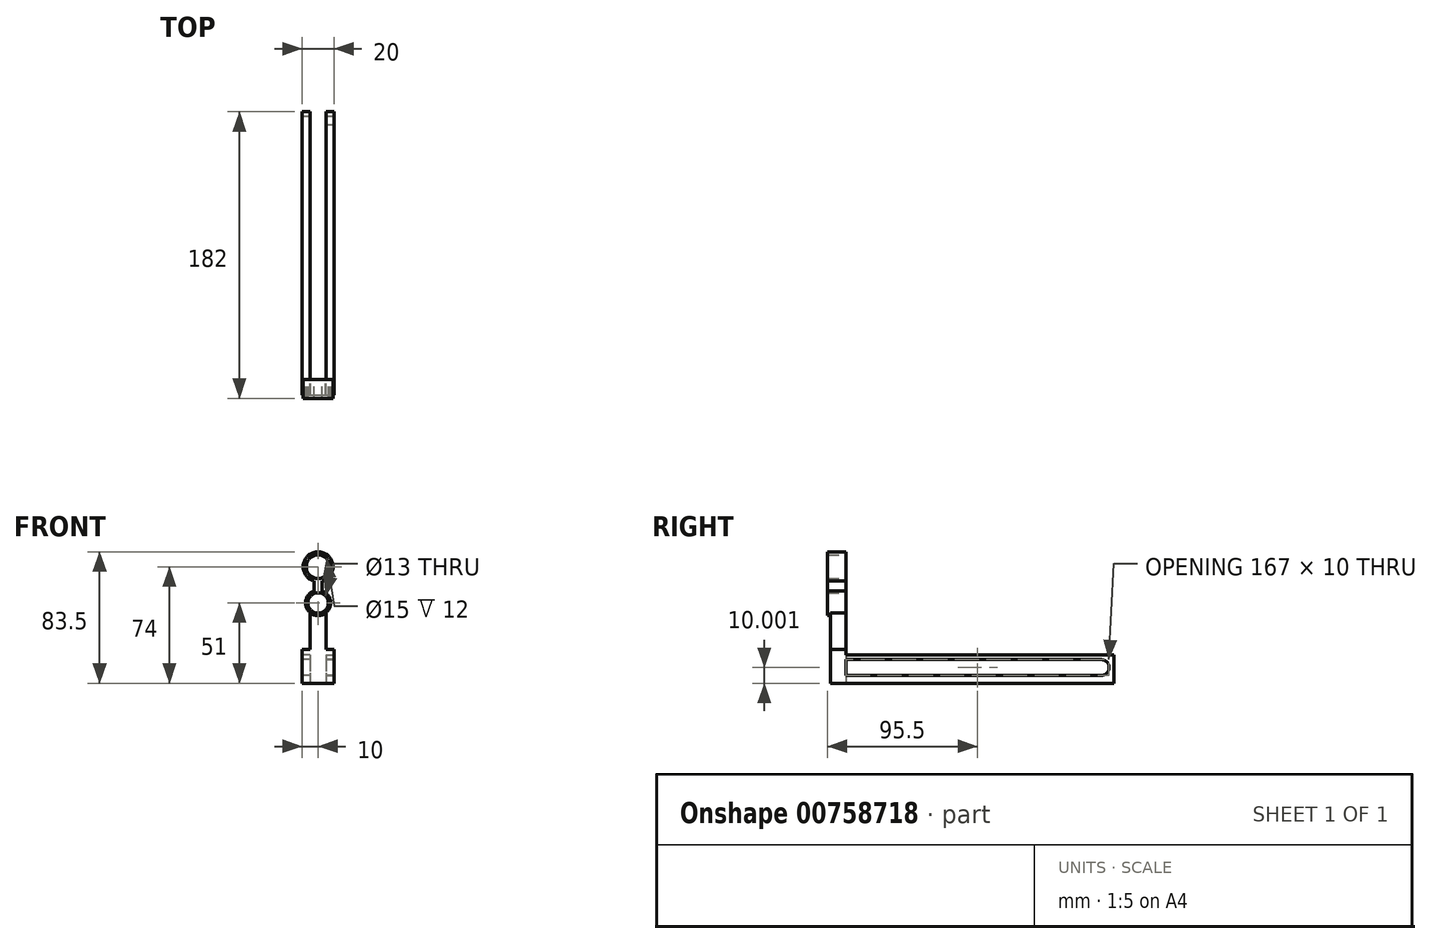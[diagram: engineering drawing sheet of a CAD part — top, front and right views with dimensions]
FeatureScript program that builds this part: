
annotation { "Feature Type Name" : "Feature", "Feature Type Description" : "" }
export const myFeature = defineFeature(function(context is Context, id is Id, definition is map)
    precondition{}
    {
        {
            var Q0;
            Q0=qCreatedBy(makeId("Front.planeOp"),FACE);
            var sketch = newSketch(context, id + "F0", { "sketchPlane" : qUnion([Q0])});
            skLineSegment(sketch, "E0", {"start": v(0, 0) * mm, "end": v(0, 23) * mm});
            skCircle(sketch, "E1", {"center": v(0, 23) * mm, "radius": 7.5 * mm});
            skCircle(sketch, "E2", {"center": v(0, 0) * mm, "radius": 6.5 * mm});
            skCircle(sketch, "E3", {"center": v(0, 23) * mm, "radius": 9.5 * mm});
            skCircle(sketch, "E4", {"center": v(0, 0) * mm, "radius": 8 * mm});
            skLineSegment(sketch, "E5", {"start": v(0, 0) * mm, "end": v(2.5, 0) * mm});
            skLineSegment(sketch, "E6", {"start": v(0, 0) * mm, "end": v(-2.5, 0) * mm});
            skLineSegment(sketch, "E7", {"start": v(-2.5, 0) * mm, "end": v(-2.5, 14.83) * mm});
            skLineSegment(sketch, "E8", {"start": v(-2.5, 14.83) * mm, "end": v(2.5, 14.83) * mm});
            skLineSegment(sketch, "E9", {"start": v(2.5, 14.83) * mm, "end": v(2.5, 0) * mm});
            skSolve(sketch);
        }
        {
            var Q0;
            Q0=makeQuery(id+"F0.imprint","IMPRINT",FACE,{"disambiguationData":[TD([[makeQuery(id+"F0.imprint","IMPRINT",EDGE,{"derivedFrom":sQuery(id+"F0.wireOp",EDGE,"E2")}),-1.0]])]});
            var Q1;
            {var subQ0=sQuery(id+"F0.wireOp",EDGE,"E3");var subQ1=sQuery(id+"F0.wireOp",EDGE,"E0");var subQ2=makeQuery(id+"F0.imprint","INTERSECT",VERTEX,{"derivedFrom":[subQ1,subQ0]});Q1=makeQuery(id+"F0.imprint","IMPRINT",FACE,{"disambiguationData":[TD([[makeQuery(id+"F0.imprint","IMPRINT",EDGE,{"disambiguationData":[TD([[subQ2,-1.0]])],"derivedFrom":subQ1}),1.0]])]});}
            var Q2;
            {var subQ0=sQuery(id+"F0.wireOp",EDGE,"E3");var subQ1=sQuery(id+"F0.wireOp",EDGE,"E0");var subQ2=makeQuery(id+"F0.imprint","INTERSECT",VERTEX,{"derivedFrom":[subQ1,subQ0]});Q2=makeQuery(id+"F0.imprint","IMPRINT",FACE,{"disambiguationData":[TD([[makeQuery(id+"F0.imprint","IMPRINT",EDGE,{"disambiguationData":[TD([[subQ2,-1.0]])],"derivedFrom":subQ1}),-1.0]])]});}
            var Q3;
            Q3=makeQuery(id+"F0.imprint","IMPRINT",FACE,{"disambiguationData":[TD([[makeQuery(id+"F0.imprint","IMPRINT",EDGE,{"derivedFrom":sQuery(id+"F0.wireOp",EDGE,"E1")}),-1.0]])]});
            var Q4;
            {var subQ0=sQuery(id+"F0.wireOp",EDGE,"E4");var subQ1=sQuery(id+"F0.wireOp",EDGE,"E0");var subQ2=makeQuery(id+"F0.imprint","INTERSECT",VERTEX,{"derivedFrom":[subQ1,subQ0]});Q4=makeQuery(id+"F0.imprint","IMPRINT",FACE,{"disambiguationData":[TD([[makeQuery(id+"F0.imprint","IMPRINT",EDGE,{"disambiguationData":[TD([[subQ2,-1.0]])],"derivedFrom":subQ1}),-1.0]])]});}
            var Q5;
            {var subQ0=sQuery(id+"F0.wireOp",EDGE,"E4");var subQ1=sQuery(id+"F0.wireOp",EDGE,"E0");var subQ2=makeQuery(id+"F0.imprint","INTERSECT",VERTEX,{"derivedFrom":[subQ1,subQ0]});Q5=makeQuery(id+"F0.imprint","IMPRINT",FACE,{"disambiguationData":[TD([[makeQuery(id+"F0.imprint","IMPRINT",EDGE,{"disambiguationData":[TD([[subQ2,-1.0]])],"derivedFrom":subQ1}),1.0]])]});}
            extrude(context, id + "F1", {"entities" : qUnion([Q0, Q1, Q2, Q3, Q4, Q5]), "depth" : 12 * mm, "offsetDistance" : 25 * mm});
        }
        {
            var Q0;
            Q0=qCreatedBy(makeId("Front.planeOp"),FACE);
            var sketch = newSketch(context, id + "F2", { "sketchPlane" : qUnion([Q0])});
            skLineSegment(sketch, "E10", {"start": v(0, 0) * mm, "end": v(0, -6.5) * mm});
            skLineSegment(sketch, "E11", {"start": v(0, -6.5) * mm, "end": v(10, -6.5) * mm});
            skLineSegment(sketch, "E12", {"start": v(0, -6.5) * mm, "end": v(-10, -6.5) * mm});
            skLineSegment(sketch, "E13", {"start": v(-10, -6.5) * mm, "end": v(-10, -51) * mm});
            skLineSegment(sketch, "E14", {"start": v(-10, -51) * mm, "end": v(10, -51) * mm});
            skLineSegment(sketch, "E15", {"start": v(10, -51) * mm, "end": v(10, -6.5) * mm});
            skLineSegment(sketch, "E16", {"start": v(-17.83, 0) * mm, "end": v(-17.83, -51) * mm});
            skLineSegment(sketch, "E17", {"start": v(-10, -51) * mm, "end": v(-17.83, -51) * mm});
            skLineSegment(sketch, "E18", {"start": v(0, -6.5) * mm, "end": v(5, -6.5) * mm});
            skLineSegment(sketch, "E19", {"start": v(5, -6.5) * mm, "end": v(5, -29.5) * mm});
            skLineSegment(sketch, "E20", {"start": v(5, -29.5) * mm, "end": v(10, -29.5) * mm});
            skLineSegment(sketch, "E21", {"start": v(-5, -6.5) * mm, "end": v(-5, -29.5) * mm});
            skLineSegment(sketch, "E22", {"start": v(-5, -29.5) * mm, "end": v(-10, -29.5) * mm});
            skSolve(sketch);
        }
        {
            var Q0;
            {var subQ0=sQuery(id+"F2.wireOp",EDGE,"E14");Q0=makeQuery(id+"F2.imprint","IMPRINT",FACE,{"disambiguationData":[TD([[makeQuery(id+"F2.imprint","IMPRINT",EDGE,{"derivedFrom":subQ0}),1.0]])]});}
            extrude(context, id + "F3", {"entities" : qUnion([Q0]), "operationType" : NewBodyOperationType.ADD, "depth" : 10 * mm, "offsetDistance" : 25 * mm});
        }
        {
            var Q0;
            Q0=qCreatedBy(makeId("Front.planeOp"),FACE);
            var sketch = newSketch(context, id + "F4", { "sketchPlane" : qUnion([Q0])});
            skLineSegment(sketch, "E23", {"start": v(0, 0) * mm, "end": v(5, 0) * mm});
            skLineSegment(sketch, "E24", {"start": v(0, 0) * mm, "end": v(-5, 0) * mm});
            skLineSegment(sketch, "E25", {"start": v(-5, 0) * mm, "end": v(-5, -46) * mm});
            skLineSegment(sketch, "E26", {"start": v(5, 0) * mm, "end": v(5, -46) * mm});
            skLineSegment(sketch, "E27", {"start": v(5, -46) * mm, "end": v(-5, -46) * mm});
            skLineSegment(sketch, "E28", {"start": v(5, -36) * mm, "end": v(-5, -36) * mm});
            skLineSegment(sketch, "E29", {"start": v(0, -36) * mm, "end": v(0, -46) * mm});
            skLineSegment(sketch, "E30", {"start": v(5, -46) * mm, "end": v(10, -46) * mm});
            skLineSegment(sketch, "E31", {"start": v(5, -36) * mm, "end": v(10, -36) * mm});
            skLineSegment(sketch, "E32", {"start": v(10, -36) * mm, "end": v(10, -46) * mm});
            skLineSegment(sketch, "E33", {"start": v(-5, -36) * mm, "end": v(-10, -36) * mm});
            skLineSegment(sketch, "E34", {"start": v(-5, -46) * mm, "end": v(-10, -46) * mm});
            skLineSegment(sketch, "E35", {"start": v(0, -36) * mm, "end": v(0, -33) * mm});
            skLineSegment(sketch, "E36", {"start": v(0, -33) * mm, "end": v(-10, -33) * mm});
            skLineSegment(sketch, "E37", {"start": v(0, -33) * mm, "end": v(10, -33) * mm});
            skLineSegment(sketch, "E38", {"start": v(10, -36) * mm, "end": v(10, -33) * mm});
            skLineSegment(sketch, "E39", {"start": v(-10, -36) * mm, "end": v(-10, -33) * mm});
            skLineSegment(sketch, "E40", {"start": v(5, -46) * mm, "end": v(5, -51) * mm});
            skLineSegment(sketch, "E41", {"start": v(5, -51) * mm, "end": v(10, -51) * mm});
            skLineSegment(sketch, "E42", {"start": v(10, -51) * mm, "end": v(10, -46) * mm});
            skLineSegment(sketch, "E43", {"start": v(-5, -46) * mm, "end": v(-5, -51) * mm});
            skLineSegment(sketch, "E44", {"start": v(-5, -51) * mm, "end": v(-10, -51) * mm});
            skLineSegment(sketch, "E45", {"start": v(-10, -51) * mm, "end": v(-10, -46) * mm});
            skSolve(sketch);
        }
        {
            var Q0;
            Q0=makeQuery(id+"F4.imprint","IMPRINT",FACE,{"disambiguationData":[TD([[makeQuery(id+"F4.imprint","IMPRINT",EDGE,{"derivedFrom":sQuery(id+"F4.wireOp",EDGE,"E30")}),-1.0]])]});
            var Q1;
            {var subQ0=sQuery(id+"F4.wireOp",EDGE,"E31");Q1=makeQuery(id+"F4.imprint","IMPRINT",FACE,{"disambiguationData":[TD([[makeQuery(id+"F4.imprint","IMPRINT",EDGE,{"derivedFrom":subQ0}),1.0]])]});}
            var Q2;
            {var subQ0=sQuery(id+"F4.wireOp",EDGE,"E33");Q2=makeQuery(id+"F4.imprint","IMPRINT",FACE,{"disambiguationData":[TD([[makeQuery(id+"F4.imprint","IMPRINT",EDGE,{"derivedFrom":subQ0}),-1.0]])]});}
            var Q3;
            {var subQ0=sQuery(id+"F4.wireOp",EDGE,"E34");Q3=makeQuery(id+"F4.imprint","IMPRINT",FACE,{"disambiguationData":[TD([[makeQuery(id+"F4.imprint","IMPRINT",EDGE,{"derivedFrom":subQ0}),1.0]])]});}
            extrude(context, id + "F5", {"entities" : qUnion([Q0, Q1, Q2, Q3]), "operationType" : NewBodyOperationType.ADD, "oppositeDirection" : true, "depth" : 170 * mm, "offsetDistance" : 25 * mm});
        }
        {
            var Q0;
            Q0=makeQuery(id+"F5.opExtrude","SWEPT_FACE",FACE,{"disambiguationData":[OSD([sQuery(id+"F4.wireOp",EDGE,"E31")])]});
            var sketch = newSketch(context, id + "F6", { "sketchPlane" : qUnion([Q0])});
            skLineSegment(sketch, "E46", {"start": v(10, -170) * mm, "end": v(10, -162) * mm});
            skLineSegment(sketch, "E47", {"start": v(10, -162) * mm, "end": v(5, -162) * mm});
            skLineSegment(sketch, "E48", {"start": v(5, -162) * mm, "end": v(5, -170) * mm});
            skLineSegment(sketch, "E49", {"start": v(5, -170) * mm, "end": v(10, -170) * mm});
            skLineSegment(sketch, "E50", {"start": v(5, -170) * mm, "end": v(-5, -170) * mm});
            skLineSegment(sketch, "E51", {"start": v(-5, -170) * mm, "end": v(-10, -170) * mm});
            skLineSegment(sketch, "E52", {"start": v(-10, -170) * mm, "end": v(-10, -162) * mm});
            skLineSegment(sketch, "E53", {"start": v(-10, -162) * mm, "end": v(-5, -162) * mm});
            skLineSegment(sketch, "E54", {"start": v(-5, -162) * mm, "end": v(-5, -170) * mm});
            skSolve(sketch);
        }
        {
            var Q0;
            Q0=makeQuery(id+"F6.imprint","IMPRINT",FACE,{"disambiguationData":[TD([[makeQuery(id+"F6.imprint","IMPRINT",EDGE,{"derivedFrom":sQuery(id+"F6.wireOp",EDGE,"E51")}),-1.0]])]});
            var Q1;
            Q1=makeQuery(id+"F6.imprint","IMPRINT",FACE,{"disambiguationData":[TD([[makeQuery(id+"F6.imprint","IMPRINT",EDGE,{"derivedFrom":sQuery(id+"F6.wireOp",EDGE,"E46")}),1.0]])]});
            extrude(context, id + "F7", {"entities" : qUnion([Q0, Q1]), "operationType" : NewBodyOperationType.ADD, "depth" : 12.7 * mm, "offsetDistance" : 25 * mm});
        }
        {
            var Q0;
            Q0=makeQuery(id+"F7.boolean.opBoolean","MERGE",FACE,{"derivedFrom":[makeQuery(id+"F5.boolean.opBoolean","MERGE",FACE,{"derivedFrom":[makeQuery(id+"F3.opExtrude","SWEPT_FACE",FACE,{"disambiguationData":[OSD([sQuery(id+"F2.wireOp",EDGE,"E13")])]}),makeQuery(id+"F5.opExtrude","SWEPT_FACE",FACE,{"disambiguationData":[OSD([sQuery(id+"F4.wireOp",EDGE,"E39")])]}),makeQuery(id+"F5.opExtrude","SWEPT_FACE",FACE,{"disambiguationData":[OSD([sQuery(id+"F4.wireOp",EDGE,"E45")])]})]}),makeQuery(id+"F7.opExtrude","SWEPT_FACE",FACE,{"disambiguationData":[OSD([sQuery(id+"F6.wireOp",EDGE,"E52")])]})]});
            var sketch = newSketch(context, id + "F8", { "sketchPlane" : qUnion([Q0])});
            skCircle(sketch, "E55", {"center": v(-162, -41) * mm, "radius": 5 * mm});
            skSolve(sketch);
        }
        {
            var Q0;
            {var subQ5=makeQuery(id+"F7.opExtrude","SWEPT_EDGE",EDGE,{"disambiguationData":[OSD([sQuery(id+"F6.wireOp",EDGE,"E52"),sQuery(id+"F6.wireOp",EDGE,"E53")])]});Q0=makeQuery(id+"F8.imprint","IMPRINT",FACE,{"disambiguationData":[TD([[makeQuery(id+"F8.imprint","IMPRINT",EDGE,{"derivedFrom":subQ5}),1.0]])]});}
            var Q1;
            {var subQ5=makeQuery(id+"F7.opExtrude","SWEPT_EDGE",EDGE,{"disambiguationData":[OSD([sQuery(id+"F6.wireOp",EDGE,"E52"),sQuery(id+"F6.wireOp",EDGE,"E53")])]});Q1=makeQuery(id+"F8.imprint","IMPRINT",FACE,{"disambiguationData":[TD([[makeQuery(id+"F8.imprint","IMPRINT",EDGE,{"derivedFrom":subQ5}),-1.0]])]});}
            extrude(context, id + "F9", {"entities" : qUnion([Q0, Q1]), "operationType" : NewBodyOperationType.REMOVE, "oppositeDirection" : true, "depth" : 25 * mm, "offsetDistance" : 25 * mm});
        }
    });
